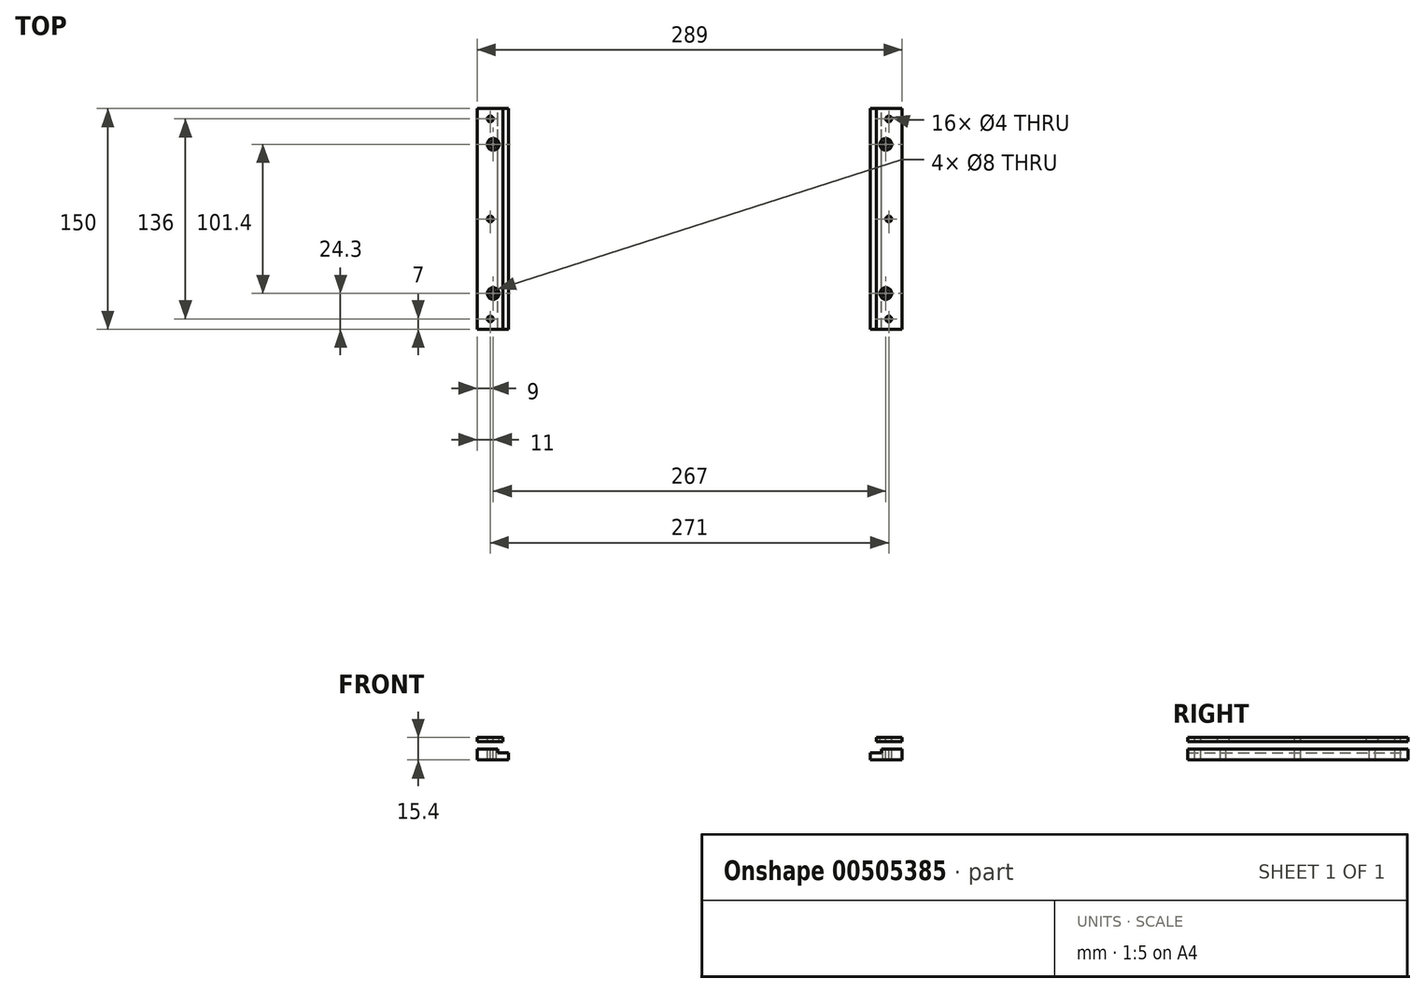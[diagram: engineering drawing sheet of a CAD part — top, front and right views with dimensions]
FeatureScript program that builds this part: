
annotation { "Feature Type Name" : "Feature", "Feature Type Description" : "" }
export const myFeature = defineFeature(function(context is Context, id is Id, definition is map)
    precondition{}
    {
        {
            var Q0;
            Q0=qCreatedBy(makeId("Front.planeOp"),FACE);
            var sketch = newSketch(context, id + "F0", { "sketchPlane" : qUnion([Q0])});
            skLineSegment(sketch, "E0", {"start": v(-130.5, 3.7) * mm, "end": v(-144.5, 3.7) * mm});
            skLineSegment(sketch, "E1", {"start": v(-144.5, 3.7) * mm, "end": v(-144.5, -3.7) * mm});
            skLineSegment(sketch, "E2", {"start": v(-144.5, -3.7) * mm, "end": v(-123, -3.7) * mm});
            skLineSegment(sketch, "E3", {"start": v(-123, -3.7) * mm, "end": v(-123, 1.3) * mm});
            skLineSegment(sketch, "E4", {"start": v(-123, 1.3) * mm, "end": v(-130.5, 1.3) * mm});
            skLineSegment(sketch, "E5", {"start": v(-130.5, 1.3) * mm, "end": v(-130.5, 3.7) * mm});
            skLineSegment(sketch, "E6.bottom", {"start": v(-144.5, 8.7) * mm, "end": v(-127, 8.7) * mm});
            skLineSegment(sketch, "E6.top", {"start": v(-144.5, 11.7) * mm, "end": v(-127, 11.7) * mm});
            skLineSegment(sketch, "E6.left", {"start": v(-144.5, 8.7) * mm, "end": v(-144.5, 11.7) * mm});
            skLineSegment(sketch, "E6.right", {"start": v(-127, 8.7) * mm, "end": v(-127, 11.7) * mm});
            skSolve(sketch);
        }
        {
            var Q0;
            Q0=makeQuery(id+"F0.imprint","IMPRINT",FACE,{"disambiguationData":[TD([[makeQuery(id+"F0.imprint","IMPRINT",EDGE,{"derivedFrom":sQuery(id+"F0.wireOp",EDGE,"E6.bottom")}),1.0]])]});
            var Q1;
            Q1=makeQuery(id+"F0.imprint","IMPRINT",FACE,{"disambiguationData":[TD([[makeQuery(id+"F0.imprint","IMPRINT",EDGE,{"derivedFrom":sQuery(id+"F0.wireOp",EDGE,"E0")}),1.0]])]});
            extrude(context, id + "F1", {"entities" : qUnion([Q0, Q1]), "endBound" : BoundingType.SYMMETRIC, "depth" : 150 * mm});
        }
        {
            var Q0;
            Q0=makeQuery(id+"F1.opExtrude","SWEPT_FACE",FACE,{"disambiguationData":[OSD([sQuery(id+"F0.wireOp",EDGE,"E6.top")])]});
            var sketch = newSketch(context, id + "F2", { "sketchPlane" : qUnion([Q0])});
            skLineSegment(sketch, "E7.0", {"start": v(-130.5, -75) * mm, "end": v(-130.5, 75) * mm, "construction": true});
            skCircle(sketch, "E8", {"center": v(-135.5, -68) * mm, "radius": 2 * mm});
            skCircle(sketch, "E9", {"center": v(-135.5, 0) * mm, "radius": 2 * mm});
            skPoint(sketch, "E9.centerSnap0", {"position": v(-130.5, 0) * mm});
            skCircle(sketch, "E10", {"center": v(-135.5, 68) * mm, "radius": 2 * mm});
            skCircle(sketch, "E11", {"center": v(-133.5, -50.7) * mm, "radius": 2 * mm});
            skCircle(sketch, "E12", {"center": v(-133.5, 50.7) * mm, "radius": 2 * mm});
            skCircle(sketch, "E13", {"center": v(-133.5, -50.7) * mm, "radius": 4 * mm});
            skCircle(sketch, "E14", {"center": v(-133.5, 50.7) * mm, "radius": 4 * mm});
            skSolve(sketch);
        }
        {
            var Q0;
            Q0=makeQuery(id+"F2.imprint","IMPRINT",FACE,{"disambiguationData":[TD([[makeQuery(id+"F2.imprint","IMPRINT",EDGE,{"derivedFrom":sQuery(id+"F2.wireOp",EDGE,"E10")}),1.0]])]});
            var Q1;
            Q1=makeQuery(id+"F2.imprint","IMPRINT",FACE,{"disambiguationData":[TD([[makeQuery(id+"F2.imprint","IMPRINT",EDGE,{"derivedFrom":sQuery(id+"F2.wireOp",EDGE,"E12")}),1.0]])]});
            var Q2;
            Q2=makeQuery(id+"F2.imprint","IMPRINT",FACE,{"disambiguationData":[TD([[makeQuery(id+"F2.imprint","IMPRINT",EDGE,{"derivedFrom":sQuery(id+"F2.wireOp",EDGE,"E9")}),1.0]])]});
            var Q3;
            Q3=makeQuery(id+"F2.imprint","IMPRINT",FACE,{"disambiguationData":[TD([[makeQuery(id+"F2.imprint","IMPRINT",EDGE,{"derivedFrom":sQuery(id+"F2.wireOp",EDGE,"E11")}),1.0]])]});
            var Q4;
            Q4=makeQuery(id+"F2.imprint","IMPRINT",FACE,{"disambiguationData":[TD([[makeQuery(id+"F2.imprint","IMPRINT",EDGE,{"derivedFrom":sQuery(id+"F2.wireOp",EDGE,"E8")}),1.0]])]});
            extrude(context, id + "F3", {"entities" : qUnion([Q0, Q1, Q2, Q3, Q4]), "operationType" : NewBodyOperationType.REMOVE, "endBound" : BoundingType.THROUGH_ALL, "oppositeDirection" : true, "depth" : 25 * mm});
        }
        {
            var Q0;
            Q0=makeQuery(id+"F2.imprint","IMPRINT",FACE,{"disambiguationData":[TD([[makeQuery(id+"F2.imprint","IMPRINT",EDGE,{"derivedFrom":sQuery(id+"F2.wireOp",EDGE,"E12")}),-1.0]])]});
            var Q1;
            Q1=makeQuery(id+"F2.imprint","IMPRINT",FACE,{"disambiguationData":[TD([[makeQuery(id+"F2.imprint","IMPRINT",EDGE,{"derivedFrom":sQuery(id+"F2.wireOp",EDGE,"E11")}),-1.0]])]});
            var Q2;
            Q2=makeQuery(id+"F1.opExtrude","SWEPT_FACE",FACE,{"disambiguationData":[OSD([sQuery(id+"F0.wireOp",EDGE,"E6.bottom")])]});
            extrude(context, id + "F4", {"entities" : qUnion([Q0, Q1]), "operationType" : NewBodyOperationType.REMOVE, "endBound" : BoundingType.UP_TO_SURFACE, "oppositeDirection" : true, "endBoundEntityFace" : qUnion([Q2]), "depth" : 25 * mm});
        }
        {
            var Q0;
            Q0=makeQuery(id+"F1.opExtrude","SWEPT_BODY",BODY,{"disambiguationData":[OSD([sQuery(id+"F0.wireOp",EDGE,"E6.bottom"),sQuery(id+"F0.wireOp",EDGE,"E6.top"),sQuery(id+"F0.wireOp",EDGE,"E6.left"),sQuery(id+"F0.wireOp",EDGE,"E6.right")])]});
            var Q1;
            Q1=makeQuery(id+"F1.opExtrude","SWEPT_BODY",BODY,{"disambiguationData":[OSD([sQuery(id+"F0.wireOp",EDGE,"E0"),sQuery(id+"F0.wireOp",EDGE,"E1"),sQuery(id+"F0.wireOp",EDGE,"E2"),sQuery(id+"F0.wireOp",EDGE,"E3"),sQuery(id+"F0.wireOp",EDGE,"E4"),sQuery(id+"F0.wireOp",EDGE,"E5")])]});
            var Q2;
            Q2=qCreatedBy(makeId("Right.planeOp"),FACE);
            mirror(context, id + "F5", {"entities" : qUnion([Q0, Q1]), "mirrorPlane" : qUnion([Q2])});
        }
    });
